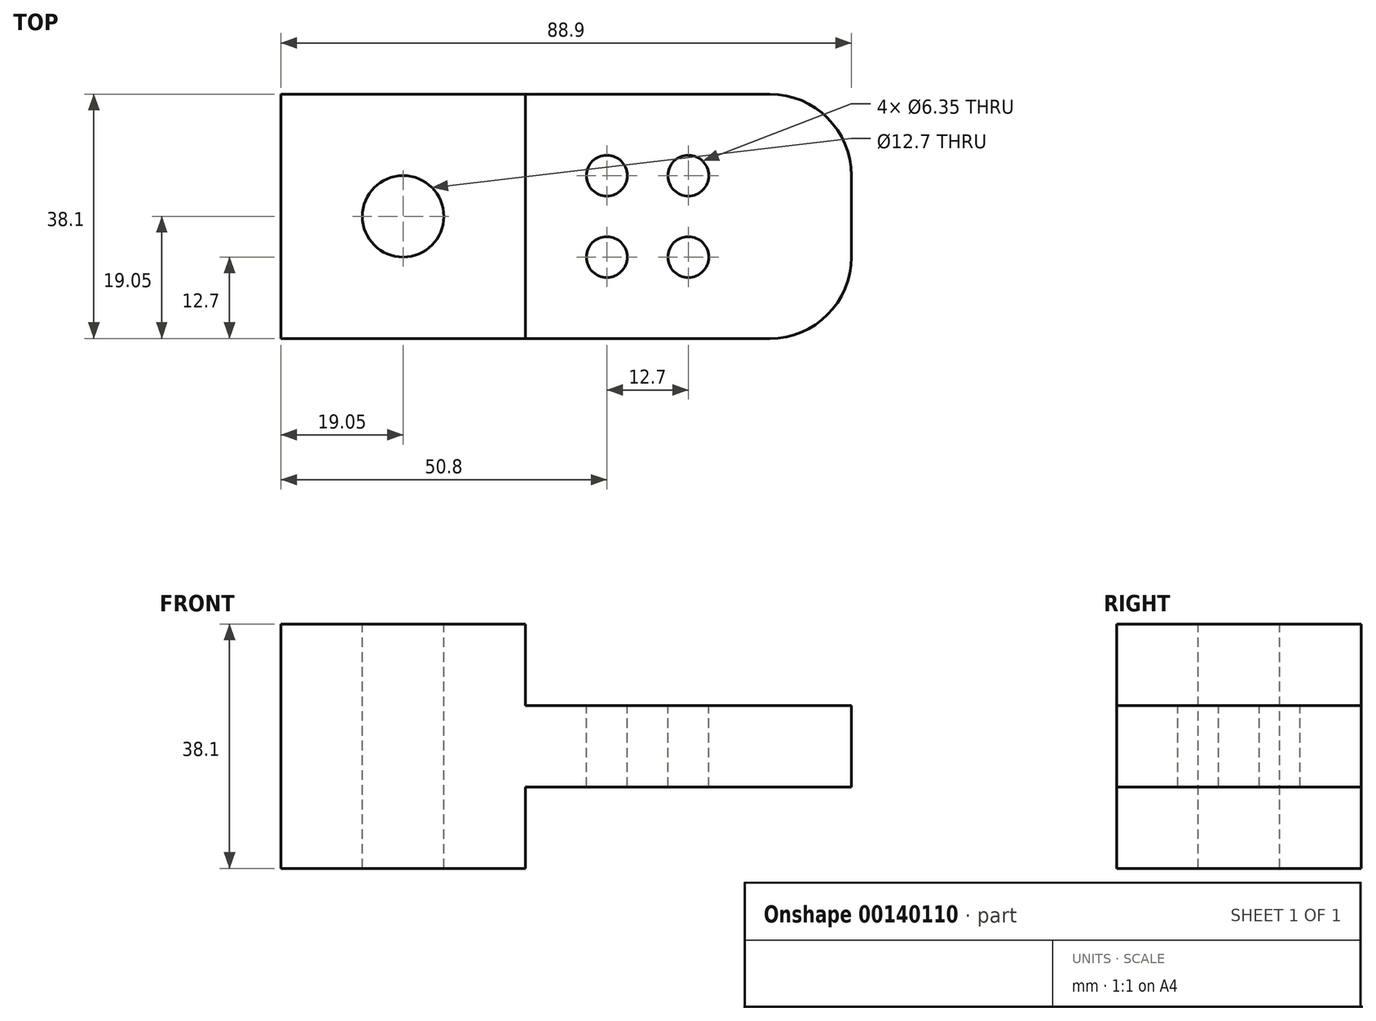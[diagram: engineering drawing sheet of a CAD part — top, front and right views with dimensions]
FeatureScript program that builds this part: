
annotation { "Feature Type Name" : "Feature", "Feature Type Description" : "" }
export const myFeature = defineFeature(function(context is Context, id is Id, definition is map)
    precondition{}
    {
        {
            var Q0;
            Q0=qCreatedBy(makeId("Front.planeOp"),FACE);
            var sketch = newSketch(context, id + "F0", { "sketchPlane" : qUnion([Q0])});
            skLineSegment(sketch, "E0", {"start": v(0, 0) * mm, "end": v(0, 38.1) * mm});
            skLineSegment(sketch, "E1", {"start": v(0, 38.1) * mm, "end": v(38.1, 38.1) * mm});
            skLineSegment(sketch, "E2", {"start": v(38.1, 38.1) * mm, "end": v(38.1, 25.4) * mm});
            skLineSegment(sketch, "E3", {"start": v(38.1, 25.4) * mm, "end": v(88.9, 25.4) * mm});
            skLineSegment(sketch, "E4", {"start": v(88.9, 25.4) * mm, "end": v(88.9, 12.7) * mm});
            skLineSegment(sketch, "E5", {"start": v(88.9, 12.7) * mm, "end": v(38.1, 12.7) * mm});
            skLineSegment(sketch, "E6", {"start": v(38.1, 12.7) * mm, "end": v(38.1, 0) * mm});
            skLineSegment(sketch, "E7", {"start": v(38.1, 0) * mm, "end": v(0, 0) * mm});
            skSolve(sketch);
        }
        {
            var Q0;
            Q0=makeQuery(id+"F0.imprint","IMPRINT",FACE,{"disambiguationData":[TD([[makeQuery(id+"F0.imprint","IMPRINT",EDGE,{"derivedFrom":sQuery(id+"F0.wireOp",EDGE,"E0")}),-1.0]])]});
            extrude(context, id + "F1", {"entities" : qUnion([Q0]), "oppositeDirection" : true, "depth" : 38.1 * mm});
        }
        {
            var Q0;
            Q0=makeQuery(id+"F1.opExtrude","SWEPT_FACE",FACE,{"disambiguationData":[OSD([sQuery(id+"F0.wireOp",EDGE,"E3")])]});
            var sketch = newSketch(context, id + "F2", { "sketchPlane" : qUnion([Q0])});
            skLineSegment(sketch, "E8", {"start": v(38.1, 38.1) * mm, "end": v(50.8, 38.1) * mm, "construction": true});
            skLineSegment(sketch, "E9", {"start": v(50.8, 38.1) * mm, "end": v(50.8, 25.4) * mm, "construction": true});
            skLineSegment(sketch, "E10", {"start": v(50.8, 25.4) * mm, "end": v(50.8, 12.7) * mm, "construction": true});
            skLineSegment(sketch, "E11", {"start": v(50.8, 12.7) * mm, "end": v(63.5, 12.7) * mm, "construction": true});
            skLineSegment(sketch, "E12", {"start": v(63.5, 12.7) * mm, "end": v(63.5, 25.4) * mm, "construction": true});
            skSolve(sketch);
        }
        {
            var Q0;
            Q0=sQuery(id+"F2.wireOp",VERTEX,"E10.start");
            var Q1;
            Q1=sQuery(id+"F2.wireOp",VERTEX,"E11.start");
            var Q2;
            Q2=sQuery(id+"F2.wireOp",VERTEX,"E11.end");
            var Q3;
            Q3=sQuery(id+"F2.wireOp",VERTEX,"E12.end");
            var Q4;
            Q4=makeQuery(id+"F1.opExtrude","SWEPT_BODY",BODY,{"disambiguationData":[OSD([sQuery(id+"F0.wireOp",EDGE,"E0"),sQuery(id+"F0.wireOp",EDGE,"E1"),sQuery(id+"F0.wireOp",EDGE,"E2"),sQuery(id+"F0.wireOp",EDGE,"E3"),sQuery(id+"F0.wireOp",EDGE,"E4"),sQuery(id+"F0.wireOp",EDGE,"E5"),sQuery(id+"F0.wireOp",EDGE,"E6"),sQuery(id+"F0.wireOp",EDGE,"E7")])]});
            hole(context, id + "F3", {"style" : HoleStyle.SIMPLE, "endStyle" : HoleEndStyle.THROUGH, "holeDiameter" : 6.35 * mm, "locations" : qUnion([Q0, Q1, Q2, Q3]), "scope" : qUnion([Q4]), "isTappedThrough" : true});
        }
        {
            var Q0;
            Q0=makeQuery(id+"F1.opExtrude","SWEPT_FACE",FACE,{"disambiguationData":[OSD([sQuery(id+"F0.wireOp",EDGE,"E1")])]});
            var sketch = newSketch(context, id + "F4", { "sketchPlane" : qUnion([Q0])});
            skLineSegment(sketch, "E13", {"start": v(19.05, 38.1) * mm, "end": v(19.05, 19.05) * mm, "construction": true});
            skPoint(sketch, "E13.endSnap0", {"position": v(0, 19.05) * mm});
            skSolve(sketch);
        }
        {
            var Q0;
            Q0=sQuery(id+"F4.wireOp",VERTEX,"E13.end");
            var Q1;
            Q1=makeQuery(id+"F1.opExtrude","SWEPT_BODY",BODY,{"disambiguationData":[OSD([sQuery(id+"F0.wireOp",EDGE,"E0"),sQuery(id+"F0.wireOp",EDGE,"E1"),sQuery(id+"F0.wireOp",EDGE,"E2"),sQuery(id+"F0.wireOp",EDGE,"E3"),sQuery(id+"F0.wireOp",EDGE,"E4"),sQuery(id+"F0.wireOp",EDGE,"E5"),sQuery(id+"F0.wireOp",EDGE,"E6"),sQuery(id+"F0.wireOp",EDGE,"E7")])]});
            hole(context, id + "F5", {"style" : HoleStyle.SIMPLE, "endStyle" : HoleEndStyle.THROUGH, "holeDiameter" : 12.7 * mm, "locations" : qUnion([Q0]), "scope" : qUnion([Q1]), "isTappedThrough" : true});
        }
        {
            var Q0;
            Q0=makeQuery(id+"F1.opExtrude","CAP_EDGE",EDGE,{"disambiguationData":[OSD([sQuery(id+"F0.wireOp",EDGE,"E4")])],"isStart":true});
            var Q1;
            Q1=makeQuery(id+"F1.opExtrude","CAP_EDGE",EDGE,{"disambiguationData":[OSD([sQuery(id+"F0.wireOp",EDGE,"E4")])],"isStart":false});
            fillet(context, id + "F6", {"entities" : qUnion([Q0, Q1]), "radius" : 12.7 * mm, "tangentPropagation" : true, "allowEdgeOverflow" : false});
        }
    });
